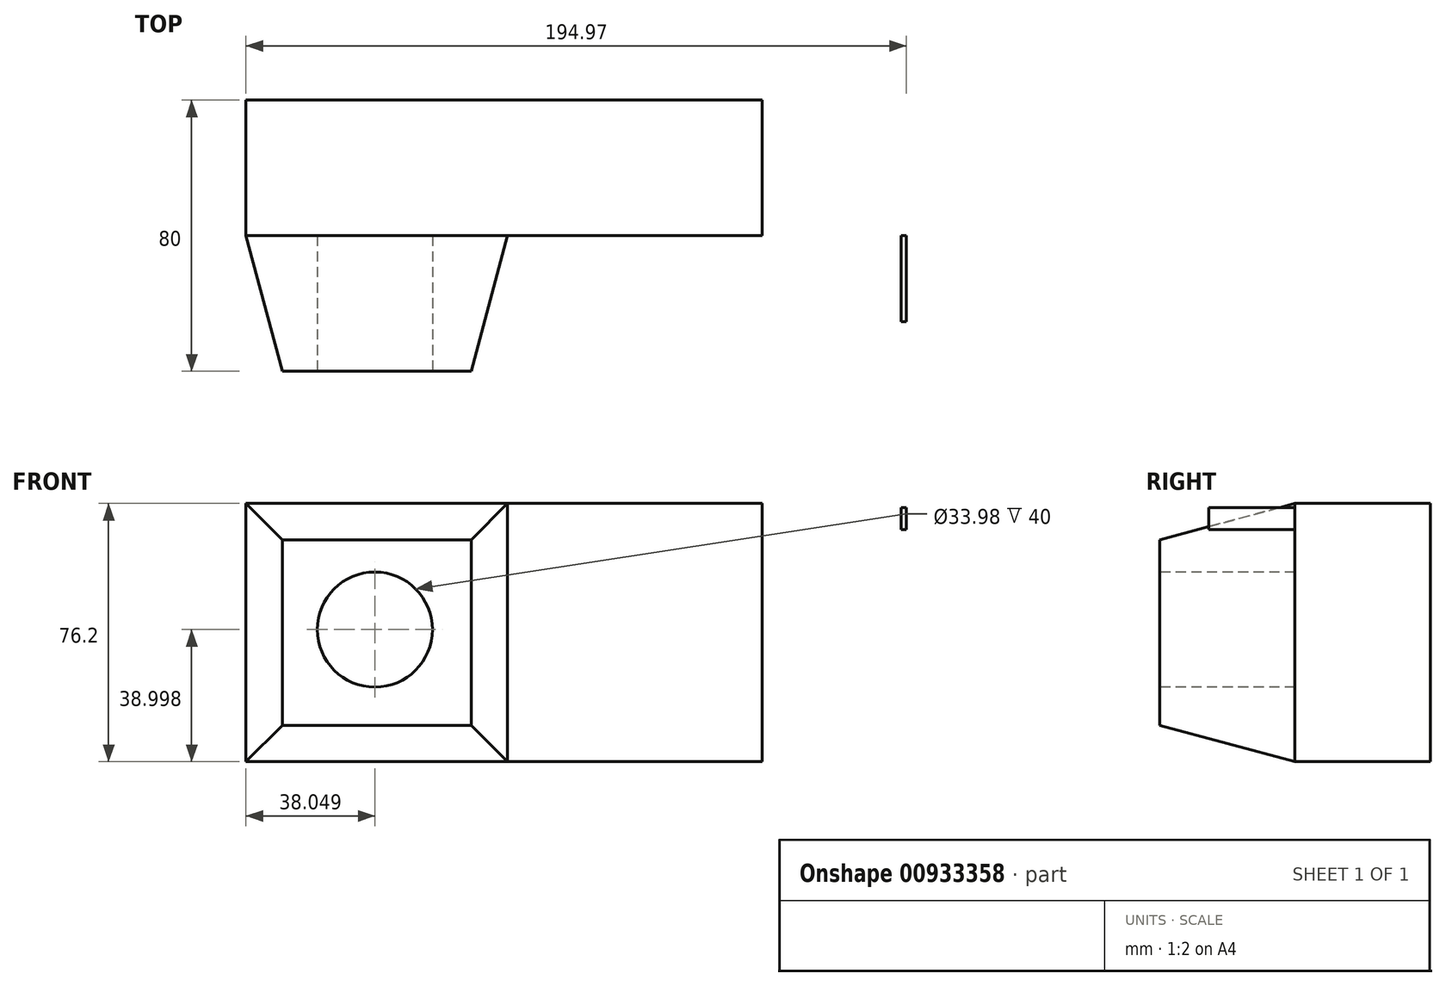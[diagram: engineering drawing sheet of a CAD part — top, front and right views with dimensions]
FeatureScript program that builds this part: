
annotation { "Feature Type Name" : "Feature", "Feature Type Description" : "" }
export const myFeature = defineFeature(function(context is Context, id is Id, definition is map)
    precondition{}
    {
        {
            var Q0;
            Q0=qCreatedBy(makeId("Front.planeOp"),FACE);
            var sketch = newSketch(context, id + "F0", { "sketchPlane" : qUnion([Q0])});
            skLineSegment(sketch, "E0.bottom", {"start": v(-77.17, 76.2) * mm, "end": v(75.23, 76.2) * mm});
            skLineSegment(sketch, "E0.top", {"start": v(-77.17, 0) * mm, "end": v(75.23, 0) * mm});
            skLineSegment(sketch, "E0.left", {"start": v(-77.17, 76.2) * mm, "end": v(-77.17, 0) * mm});
            skLineSegment(sketch, "E0.right", {"start": v(75.23, 76.2) * mm, "end": v(75.23, 0) * mm});
            skSolve(sketch);
        }
        {
            var Q0;
            Q0=makeQuery(id+"F0.imprint","IMPRINT",FACE,{"disambiguationData":[TD([[makeQuery(id+"F0.imprint","IMPRINT",EDGE,{"derivedFrom":sQuery(id+"F0.wireOp",EDGE,"E0.bottom")}),-1.0]])]});
            extrude(context, id + "F1", {"entities" : qUnion([Q0]), "depth" : 40 * mm, "offsetDistance" : 25.4 * mm});
        }
        {
            var Q0;
            Q0=makeQuery(id+"F1.opExtrude","CAP_FACE",FACE,{"disambiguationData":[OSD([sQuery(id+"F0.wireOp",EDGE,"E0.bottom"),sQuery(id+"F0.wireOp",EDGE,"E0.top"),sQuery(id+"F0.wireOp",EDGE,"E0.left"),sQuery(id+"F0.wireOp",EDGE,"E0.right")])],"isStart":false});
            var sketch = newSketch(context, id + "F2", { "sketchPlane" : qUnion([Q0])});
            skLineSegment(sketch, "E1.bottom", {"start": v(117.8, 68.49) * mm, "end": v(116.17, 68.49) * mm});
            skLineSegment(sketch, "E1.top", {"start": v(117.8, 75) * mm, "end": v(116.17, 75) * mm});
            skLineSegment(sketch, "E1.left", {"start": v(117.8, 68.49) * mm, "end": v(117.8, 75) * mm});
            skLineSegment(sketch, "E1.right", {"start": v(116.17, 68.49) * mm, "end": v(116.17, 75) * mm});
            skSolve(sketch);
        }
        {
            var Q0;
            Q0 = qSketchRegion(id + "F2", true);
            extrude(context, id + "F3", {"entities" : qUnion([Q0]), "depth" : 25.4 * mm, "offsetDistance" : 25.4 * mm});
        }
        {
            var Q0;
            Q0=makeQuery(id+"F1.opExtrude","CAP_FACE",FACE,{"disambiguationData":[OSD([sQuery(id+"F0.wireOp",EDGE,"E0.bottom"),sQuery(id+"F0.wireOp",EDGE,"E0.top"),sQuery(id+"F0.wireOp",EDGE,"E0.left"),sQuery(id+"F0.wireOp",EDGE,"E0.right")])],"isStart":false});
            var sketch = newSketch(context, id + "F4", { "sketchPlane" : qUnion([Q0])});
            skLineSegment(sketch, "E2.bottom", {"start": v(-77.17, 76.2) * mm, "end": v(0, 76.2) * mm});
            skLineSegment(sketch, "E2.top", {"start": v(-77.17, 0) * mm, "end": v(0, 0) * mm});
            skLineSegment(sketch, "E2.left", {"start": v(-77.17, 76.2) * mm, "end": v(-77.17, 0) * mm});
            skLineSegment(sketch, "E2.right", {"start": v(0, 76.2) * mm, "end": v(0, 0) * mm});
            skSolve(sketch);
        }
        {
            var Q0;
            Q0=makeQuery(id+"F4.imprint","IMPRINT",FACE,{"disambiguationData":[TD([[makeQuery(id+"F4.imprint","IMPRINT",EDGE,{"derivedFrom":sQuery(id+"F4.wireOp",EDGE,"E2.bottom")}),-1.0]])]});
            extrude(context, id + "F5", {"entities" : qUnion([Q0]), "operationType" : NewBodyOperationType.ADD, "depth" : 40 * mm, "offsetDistance" : 25.4 * mm, "hasDraft" : true, "draftAngle" : 15 * degree, "draftPullDirection" : true});
        }
        {
            var Q0;
            Q0=makeQuery(id+"F5.opExtrude","CAP_FACE",FACE,{"disambiguationData":[OSD([sQuery(id+"F4.wireOp",EDGE,"E2.bottom"),sQuery(id+"F4.wireOp",EDGE,"E2.top"),sQuery(id+"F4.wireOp",EDGE,"E2.left"),sQuery(id+"F4.wireOp",EDGE,"E2.right")])],"isStart":false});
            var sketch = newSketch(context, id + "F6", { "sketchPlane" : qUnion([Q0])});
            skCircle(sketch, "E3", {"center": v(-39.12, 39) * mm, "radius": 17 * mm});
            skSolve(sketch);
        }
        {
            var Q0;
            Q0=makeQuery(id+"F6.imprint","IMPRINT",FACE,{"disambiguationData":[TD([[makeQuery(id+"F6.imprint","IMPRINT",EDGE,{"derivedFrom":sQuery(id+"F6.wireOp",EDGE,"E3")}),1.0]])]});
            extrude(context, id + "F7", {"entities" : qUnion([Q0]), "operationType" : NewBodyOperationType.REMOVE, "oppositeDirection" : true, "depth" : 40 * mm, "offsetDistance" : 25.4 * mm});
        }
    });
